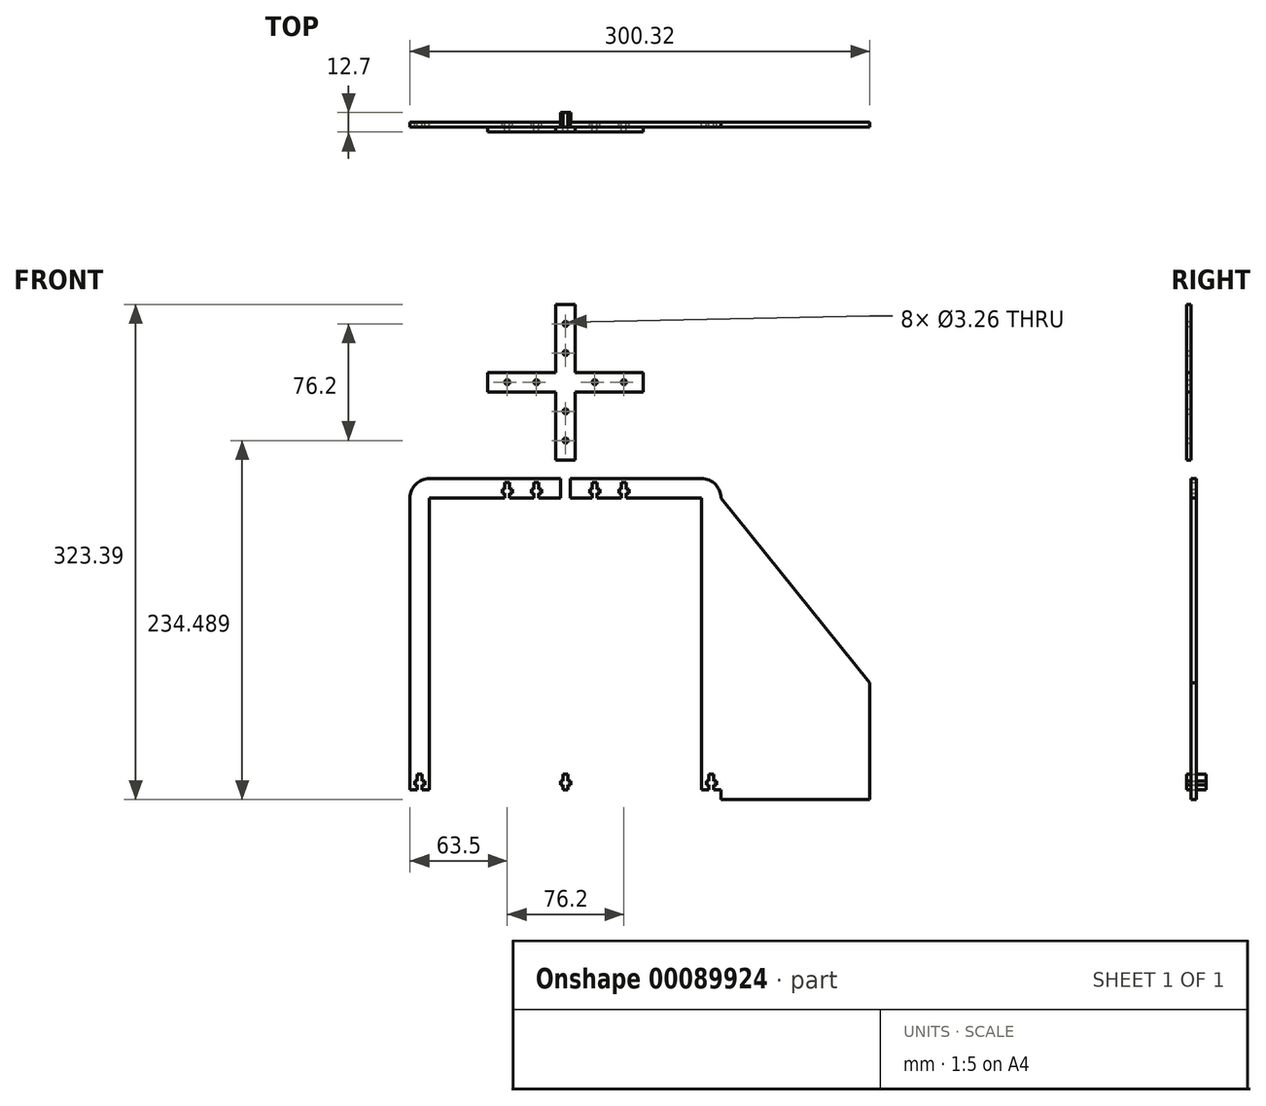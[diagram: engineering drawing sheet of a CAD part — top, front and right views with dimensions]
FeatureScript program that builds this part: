
annotation { "Feature Type Name" : "Feature", "Feature Type Description" : "" }
export const myFeature = defineFeature(function(context is Context, id is Id, definition is map)
    precondition{}
    {
        {
            var Q0;
            Q0=qCreatedBy(makeId("Top.planeOp"),FACE);
            var sketch = newSketch(context, id + "F0", { "sketchPlane" : qUnion([Q0])});
            skCircle(sketch, "E0", {"center": v(0, 0) * mm, "radius": 101.6 * mm});
            skSolve(sketch);
        }
        {
            var Q0;
            Q0=qCreatedBy(makeId("Front.planeOp"),FACE);
            var sketch = newSketch(context, id + "F1", { "sketchPlane" : qUnion([Q0])});
            skLineSegment(sketch, "E1", {"start": v(-101.6, 190.5) * mm, "end": v(-101.6, 0) * mm});
            skLineSegment(sketch, "E2", {"start": v(-88.9, 203.2) * mm, "end": v(-3.18, 203.2) * mm});
            skLineSegment(sketch, "E3", {"start": v(-3.18, 203.2) * mm, "end": v(-3.18, 190.5) * mm});
            skLineSegment(sketch, "E4", {"start": v(-3.18, 190.5) * mm, "end": v(-76.2, 190.5) * mm});
            skLineSegment(sketch, "E5", {"start": v(-88.9, 177.8) * mm, "end": v(-88.9, 0) * mm});
            skLineSegment(sketch, "E6", {"start": v(-88.9, 0) * mm, "end": v(-101.6, 0) * mm});
            skPoint(sketch, "E7.visualSharp", {"position": v(-88.9, 190.5) * mm});
            skPoint(sketch, "E8.visualSharp", {"position": v(-101.6, 203.2) * mm});
            skArc(sketch, "E8.filletArc", {"start": v(-88.9, 203.2) * mm, "mid": v(-97.88, 199.48) * mm, "end": v(-101.6, 190.5) * mm});
            skPoint(sketch, "E9.endSnap0", {"position": v(-95.25, 0) * mm});
            skLineSegment(sketch, "E10", {"start": v(-76.2, 190.5) * mm, "end": v(-88.9, 190.5) * mm});
            skLineSegment(sketch, "E11", {"start": v(-88.9, 177.8) * mm, "end": v(-88.9, 190.5) * mm});
            skSolve(sketch);
        }
        {
            var Q0;
            Q0=qCreatedBy(makeId("Front.planeOp"),FACE);
            var sketch = newSketch(context, id + "F2", { "sketchPlane" : qUnion([Q0])});
            skLineSegment(sketch, "E12", {"start": v(0, 0) * mm, "end": v(1.63, 0) * mm});
            skLineSegment(sketch, "E13", {"start": v(1.63, 0) * mm, "end": v(1.63, 3.18) * mm});
            skLineSegment(sketch, "E14", {"start": v(1.63, 3.18) * mm, "end": v(3.3, 3.18) * mm});
            skLineSegment(sketch, "E15", {"start": v(3.3, 3.18) * mm, "end": v(3.3, 5.72) * mm});
            skLineSegment(sketch, "E16", {"start": v(3.3, 5.72) * mm, "end": v(1.63, 5.72) * mm});
            skLineSegment(sketch, "E17", {"start": v(1.63, 5.72) * mm, "end": v(1.63, 10.16) * mm});
            skLineSegment(sketch, "E18", {"start": v(1.63, 10.16) * mm, "end": v(0, 10.16) * mm});
            skLineSegment(sketch, "E19.MirrorCS", {"start": v(-1.63, 0) * mm, "end": v(-1.63, 3.18) * mm});
            skLineSegment(sketch, "E20.MirrorCS", {"start": v(-1.63, 3.18) * mm, "end": v(-3.3, 3.18) * mm});
            skLineSegment(sketch, "E21.MirrorCS", {"start": v(-3.3, 3.18) * mm, "end": v(-3.3, 5.72) * mm});
            skLineSegment(sketch, "E22.MirrorCS", {"start": v(-3.3, 5.72) * mm, "end": v(-1.63, 5.72) * mm});
            skLineSegment(sketch, "E23.MirrorCS", {"start": v(-1.63, 10.16) * mm, "end": v(0, 10.16) * mm});
            skLineSegment(sketch, "E24.MirrorCS", {"start": v(-1.63, 5.72) * mm, "end": v(-1.63, 10.16) * mm});
            skLineSegment(sketch, "E25", {"start": v(0, 0) * mm, "end": v(-1.63, 0) * mm});
            skSolve(sketch);
        }
        {
            var Q0;
            Q0=makeQuery(id+"F2.imprint","IMPRINT",FACE,{"disambiguationData":[TD([[makeQuery(id+"F2.imprint","IMPRINT",EDGE,{"derivedFrom":sQuery(id+"F2.wireOp",EDGE,"E12")}),1.0]])]});
            extrude(context, id + "F3", {"entities" : qUnion([Q0]), "endBound" : BoundingType.SYMMETRIC, "depth" : 12.7 * mm});
        }
        {
            var Q0;
            Q0=makeQuery(id+"F1.imprint","IMPRINT",FACE,{"disambiguationData":[TD([[makeQuery(id+"F1.imprint","IMPRINT",EDGE,{"derivedFrom":sQuery(id+"F1.wireOp",EDGE,"E1")}),1.0]])]});
            extrude(context, id + "F4", {"entities" : qUnion([Q0]), "depth" : 3.17 * mm});
        }
        {
            var Q0;
            Q0=makeQuery(id+"F3.opExtrude","SWEPT_BODY",BODY,{"disambiguationData":[OSD([sQuery(id+"F2.wireOp",EDGE,"E12"),sQuery(id+"F2.wireOp",EDGE,"E13"),sQuery(id+"F2.wireOp",EDGE,"E14"),sQuery(id+"F2.wireOp",EDGE,"E15"),sQuery(id+"F2.wireOp",EDGE,"E16"),sQuery(id+"F2.wireOp",EDGE,"E17"),sQuery(id+"F2.wireOp",EDGE,"E18"),sQuery(id+"F2.wireOp",EDGE,"E19.MirrorCS"),sQuery(id+"F2.wireOp",EDGE,"E20.MirrorCS"),sQuery(id+"F2.wireOp",EDGE,"E21.MirrorCS"),sQuery(id+"F2.wireOp",EDGE,"E22.MirrorCS"),sQuery(id+"F2.wireOp",EDGE,"E23.MirrorCS"),sQuery(id+"F2.wireOp",EDGE,"E24.MirrorCS"),sQuery(id+"F2.wireOp",EDGE,"E25")])]});
            transform(context, id + "F5", {"entities" : qUnion([Q0]), "transformType" : TransformType.TRANSLATION_3D, "dx" : -95.25 * mm, "dy" : 0 * mm, "dz" : 0 * mm, "makeCopy" : true});
        }
        {
            var Q0;
            Q0=makeQuery(id+"F5.opPattern","COPY",BODY,{"derivedFrom":makeQuery(id+"F3.opExtrude","SWEPT_BODY",BODY,{"disambiguationData":[OSD([sQuery(id+"F2.wireOp",EDGE,"E12"),sQuery(id+"F2.wireOp",EDGE,"E13"),sQuery(id+"F2.wireOp",EDGE,"E14"),sQuery(id+"F2.wireOp",EDGE,"E15"),sQuery(id+"F2.wireOp",EDGE,"E16"),sQuery(id+"F2.wireOp",EDGE,"E17"),sQuery(id+"F2.wireOp",EDGE,"E18"),sQuery(id+"F2.wireOp",EDGE,"E19.MirrorCS"),sQuery(id+"F2.wireOp",EDGE,"E20.MirrorCS"),sQuery(id+"F2.wireOp",EDGE,"E21.MirrorCS"),sQuery(id+"F2.wireOp",EDGE,"E22.MirrorCS"),sQuery(id+"F2.wireOp",EDGE,"E23.MirrorCS"),sQuery(id+"F2.wireOp",EDGE,"E24.MirrorCS"),sQuery(id+"F2.wireOp",EDGE,"E25")])]}),"instanceName":"1"});
            var Q1;
            Q1=makeQuery(id+"F4.opExtrude","SWEPT_BODY",BODY,{"disambiguationData":[OSD([sQuery(id+"F1.wireOp",EDGE,"E1"),sQuery(id+"F1.wireOp",EDGE,"E2"),sQuery(id+"F1.wireOp",EDGE,"E3"),sQuery(id+"F1.wireOp",EDGE,"E4"),sQuery(id+"F1.wireOp",EDGE,"E5"),sQuery(id+"F1.wireOp",EDGE,"E6"),sQuery(id+"F1.wireOp",EDGE,"E7.filletArc"),sQuery(id+"F1.wireOp",EDGE,"E8.filletArc")])]});
            booleanBodies(context, id + "F6", {"operationType" : BooleanOperationType.SUBTRACTION, "tools" : qUnion([Q0]), "targets" : qUnion([Q1])});
        }
        {
            var Q0;
            Q0=makeQuery(id+"F3.opExtrude","SWEPT_BODY",BODY,{"disambiguationData":[OSD([sQuery(id+"F2.wireOp",EDGE,"E12"),sQuery(id+"F2.wireOp",EDGE,"E13"),sQuery(id+"F2.wireOp",EDGE,"E14"),sQuery(id+"F2.wireOp",EDGE,"E15"),sQuery(id+"F2.wireOp",EDGE,"E16"),sQuery(id+"F2.wireOp",EDGE,"E17"),sQuery(id+"F2.wireOp",EDGE,"E18"),sQuery(id+"F2.wireOp",EDGE,"E19.MirrorCS"),sQuery(id+"F2.wireOp",EDGE,"E20.MirrorCS"),sQuery(id+"F2.wireOp",EDGE,"E21.MirrorCS"),sQuery(id+"F2.wireOp",EDGE,"E22.MirrorCS"),sQuery(id+"F2.wireOp",EDGE,"E23.MirrorCS"),sQuery(id+"F2.wireOp",EDGE,"E24.MirrorCS"),sQuery(id+"F2.wireOp",EDGE,"E25")])]});
            transform(context, id + "F7", {"entities" : qUnion([Q0]), "transformType" : TransformType.TRANSLATION_3D, "dx" : -19.05 * mm, "dy" : 0 * mm, "dz" : 190.5 * mm, "makeCopy" : true});
        }
        {
            var Q0;
            Q0=makeQuery(id+"F7.opPattern","COPY",BODY,{"derivedFrom":makeQuery(id+"F3.opExtrude","SWEPT_BODY",BODY,{"disambiguationData":[OSD([sQuery(id+"F2.wireOp",EDGE,"E12"),sQuery(id+"F2.wireOp",EDGE,"E13"),sQuery(id+"F2.wireOp",EDGE,"E14"),sQuery(id+"F2.wireOp",EDGE,"E15"),sQuery(id+"F2.wireOp",EDGE,"E16"),sQuery(id+"F2.wireOp",EDGE,"E17"),sQuery(id+"F2.wireOp",EDGE,"E18"),sQuery(id+"F2.wireOp",EDGE,"E19.MirrorCS"),sQuery(id+"F2.wireOp",EDGE,"E20.MirrorCS"),sQuery(id+"F2.wireOp",EDGE,"E21.MirrorCS"),sQuery(id+"F2.wireOp",EDGE,"E22.MirrorCS"),sQuery(id+"F2.wireOp",EDGE,"E23.MirrorCS"),sQuery(id+"F2.wireOp",EDGE,"E24.MirrorCS"),sQuery(id+"F2.wireOp",EDGE,"E25")])]}),"instanceName":"1"});
            var Q1;
            Q1=makeQuery(id+"F4.opExtrude","SWEPT_BODY",BODY,{"disambiguationData":[OSD([sQuery(id+"F1.wireOp",EDGE,"E1"),sQuery(id+"F1.wireOp",EDGE,"E2"),sQuery(id+"F1.wireOp",EDGE,"E3"),sQuery(id+"F1.wireOp",EDGE,"E4"),sQuery(id+"F1.wireOp",EDGE,"E5"),sQuery(id+"F1.wireOp",EDGE,"E6"),sQuery(id+"F1.wireOp",EDGE,"E7.filletArc"),sQuery(id+"F1.wireOp",EDGE,"E8.filletArc")])]});
            booleanBodies(context, id + "F8", {"operationType" : BooleanOperationType.SUBTRACTION, "tools" : qUnion([Q0]), "targets" : qUnion([Q1])});
        }
        {
            var Q0;
            Q0=makeQuery(id+"F3.opExtrude","SWEPT_BODY",BODY,{"disambiguationData":[OSD([sQuery(id+"F2.wireOp",EDGE,"E12"),sQuery(id+"F2.wireOp",EDGE,"E13"),sQuery(id+"F2.wireOp",EDGE,"E14"),sQuery(id+"F2.wireOp",EDGE,"E15"),sQuery(id+"F2.wireOp",EDGE,"E16"),sQuery(id+"F2.wireOp",EDGE,"E17"),sQuery(id+"F2.wireOp",EDGE,"E18"),sQuery(id+"F2.wireOp",EDGE,"E19.MirrorCS"),sQuery(id+"F2.wireOp",EDGE,"E20.MirrorCS"),sQuery(id+"F2.wireOp",EDGE,"E21.MirrorCS"),sQuery(id+"F2.wireOp",EDGE,"E22.MirrorCS"),sQuery(id+"F2.wireOp",EDGE,"E23.MirrorCS"),sQuery(id+"F2.wireOp",EDGE,"E24.MirrorCS"),sQuery(id+"F2.wireOp",EDGE,"E25")])]});
            transform(context, id + "F9", {"entities" : qUnion([Q0]), "transformType" : TransformType.TRANSLATION_3D, "dx" : -38.1 * mm, "dy" : 0 * mm, "dz" : 190.5 * mm, "makeCopy" : true});
        }
        {
            var Q0;
            Q0=makeQuery(id+"F9.opPattern","COPY",BODY,{"derivedFrom":makeQuery(id+"F3.opExtrude","SWEPT_BODY",BODY,{"disambiguationData":[OSD([sQuery(id+"F2.wireOp",EDGE,"E12"),sQuery(id+"F2.wireOp",EDGE,"E13"),sQuery(id+"F2.wireOp",EDGE,"E14"),sQuery(id+"F2.wireOp",EDGE,"E15"),sQuery(id+"F2.wireOp",EDGE,"E16"),sQuery(id+"F2.wireOp",EDGE,"E17"),sQuery(id+"F2.wireOp",EDGE,"E18"),sQuery(id+"F2.wireOp",EDGE,"E19.MirrorCS"),sQuery(id+"F2.wireOp",EDGE,"E20.MirrorCS"),sQuery(id+"F2.wireOp",EDGE,"E21.MirrorCS"),sQuery(id+"F2.wireOp",EDGE,"E22.MirrorCS"),sQuery(id+"F2.wireOp",EDGE,"E23.MirrorCS"),sQuery(id+"F2.wireOp",EDGE,"E24.MirrorCS"),sQuery(id+"F2.wireOp",EDGE,"E25")])]}),"instanceName":"1"});
            var Q1;
            Q1=makeQuery(id+"F4.opExtrude","SWEPT_BODY",BODY,{"disambiguationData":[OSD([sQuery(id+"F1.wireOp",EDGE,"E1"),sQuery(id+"F1.wireOp",EDGE,"E2"),sQuery(id+"F1.wireOp",EDGE,"E3"),sQuery(id+"F1.wireOp",EDGE,"E4"),sQuery(id+"F1.wireOp",EDGE,"E5"),sQuery(id+"F1.wireOp",EDGE,"E6"),sQuery(id+"F1.wireOp",EDGE,"E7.filletArc"),sQuery(id+"F1.wireOp",EDGE,"E8.filletArc")])]});
            booleanBodies(context, id + "F10", {"operationType" : BooleanOperationType.SUBTRACTION, "tools" : qUnion([Q0]), "targets" : qUnion([Q1])});
        }
        {
            var Q0;
            Q0=makeQuery(id+"F4.opExtrude","SWEPT_BODY",BODY,{"disambiguationData":[OSD([sQuery(id+"F1.wireOp",EDGE,"E1"),sQuery(id+"F1.wireOp",EDGE,"E2"),sQuery(id+"F1.wireOp",EDGE,"E3"),sQuery(id+"F1.wireOp",EDGE,"E4"),sQuery(id+"F1.wireOp",EDGE,"E5"),sQuery(id+"F1.wireOp",EDGE,"E6"),sQuery(id+"F1.wireOp",EDGE,"E8.filletArc"),sQuery(id+"F1.wireOp",EDGE,"E10"),sQuery(id+"F1.wireOp",EDGE,"E11")])]});
            var Q1;
            Q1=qCreatedBy(makeId("Right.planeOp"),FACE);
            mirror(context, id + "F11", {"entities" : qUnion([Q0]), "mirrorPlane" : qUnion([Q1])});
        }
        {
            var Q0;
            Q0=makeQuery(id+"F11.opPattern","COPY",FACE,{"derivedFrom":makeQuery(id+"F4.opExtrude","CAP_FACE",FACE,{"disambiguationData":[OSD([sQuery(id+"F1.wireOp",EDGE,"E1"),sQuery(id+"F1.wireOp",EDGE,"E2"),sQuery(id+"F1.wireOp",EDGE,"E3"),sQuery(id+"F1.wireOp",EDGE,"E4"),sQuery(id+"F1.wireOp",EDGE,"E5"),sQuery(id+"F1.wireOp",EDGE,"E6"),sQuery(id+"F1.wireOp",EDGE,"E8.filletArc"),sQuery(id+"F1.wireOp",EDGE,"E10"),sQuery(id+"F1.wireOp",EDGE,"E11")])],"isStart":false}),"instanceName":"1"});
            var sketch = newSketch(context, id + "F12", { "sketchPlane" : qUnion([Q0])});
            skLineSegment(sketch, "E26", {"start": v(101.6, 190.5) * mm, "end": v(198.72, 69.85) * mm});
            skLineSegment(sketch, "E27", {"start": v(198.72, 69.85) * mm, "end": v(198.72, 0) * mm});
            skLineSegment(sketch, "E28", {"start": v(198.72, 0) * mm, "end": v(198.72, -6.35) * mm});
            skLineSegment(sketch, "E29", {"start": v(198.72, -6.35) * mm, "end": v(101.6, -6.35) * mm});
            skLineSegment(sketch, "E30", {"start": v(101.6, -6.35) * mm, "end": v(101.6, 0) * mm});
            skLineSegment(sketch, "E31", {"start": v(101.6, 0) * mm, "end": v(101.6, 190.5) * mm});
            skSolve(sketch);
        }
        {
            var Q0;
            Q0=makeQuery(id+"F12.imprint","IMPRINT",FACE,{"disambiguationData":[TD([[makeQuery(id+"F12.imprint","IMPRINT",EDGE,{"derivedFrom":sQuery(id+"F12.wireOp",EDGE,"E26")}),-1.0]])]});
            extrude(context, id + "F13", {"entities" : qUnion([Q0]), "operationType" : NewBodyOperationType.ADD, "oppositeDirection" : true, "depth" : 3.17 * mm});
        }
        {
            var Q0;
            Q0=makeQuery(id+"F4.opExtrude","CAP_FACE",FACE,{"disambiguationData":[OSD([sQuery(id+"F1.wireOp",EDGE,"E1"),sQuery(id+"F1.wireOp",EDGE,"E2"),sQuery(id+"F1.wireOp",EDGE,"E3"),sQuery(id+"F1.wireOp",EDGE,"E4"),sQuery(id+"F1.wireOp",EDGE,"E5"),sQuery(id+"F1.wireOp",EDGE,"E6"),sQuery(id+"F1.wireOp",EDGE,"E8.filletArc"),sQuery(id+"F1.wireOp",EDGE,"E10"),sQuery(id+"F1.wireOp",EDGE,"E11")])],"isStart":false});
            var sketch = newSketch(context, id + "F14", { "sketchPlane" : qUnion([Q0])});
            skLineSegment(sketch, "E32", {"start": v(-19.05, 200.66) * mm, "end": v(-19.05, 336.22) * mm, "construction": true});
            skLineSegment(sketch, "E33", {"start": v(-38.1, 200.66) * mm, "end": v(-38.1, 336.22) * mm, "construction": true});
            skLineSegment(sketch, "E34", {"start": v(0, 259.89) * mm, "end": v(-50.8, 259.89) * mm});
            skLineSegment(sketch, "E35", {"start": v(-50.8, 259.89) * mm, "end": v(-50.8, 272.59) * mm});
            skLineSegment(sketch, "E36", {"start": v(-50.8, 272.59) * mm, "end": v(0, 272.59) * mm});
            skLineSegment(sketch, "E37", {"start": v(-50.8, 266.24) * mm, "end": v(-2.03, 266.24) * mm, "construction": true});
            skCircle(sketch, "E38", {"center": v(-38.1, 266.24) * mm, "radius": 1.63 * mm});
            skCircle(sketch, "E39", {"center": v(-19.05, 266.24) * mm, "radius": 1.63 * mm});
            skLineSegment(sketch, "E40.1.0", {"start": v(6.35, 266.24) * mm, "end": v(6.35, 215.44) * mm});
            skLineSegment(sketch, "E40.1.1", {"start": v(6.35, 215.44) * mm, "end": v(-6.35, 215.44) * mm});
            skLineSegment(sketch, "E40.1.2", {"start": v(-6.35, 215.44) * mm, "end": v(-6.35, 266.24) * mm});
            skCircle(sketch, "E40.1.3", {"center": v(0, 228.14) * mm, "radius": 1.63 * mm});
            skCircle(sketch, "E40.1.4", {"center": v(0, 247.19) * mm, "radius": 1.63 * mm});
            skLineSegment(sketch, "E40.2.0", {"start": v(0, 272.59) * mm, "end": v(50.8, 272.59) * mm});
            skLineSegment(sketch, "E40.2.1", {"start": v(50.8, 272.59) * mm, "end": v(50.8, 259.89) * mm});
            skLineSegment(sketch, "E40.2.2", {"start": v(50.8, 259.89) * mm, "end": v(0, 259.89) * mm});
            skCircle(sketch, "E40.2.3", {"center": v(38.1, 266.24) * mm, "radius": 1.63 * mm});
            skCircle(sketch, "E40.2.4", {"center": v(19.05, 266.24) * mm, "radius": 1.63 * mm});
            skLineSegment(sketch, "E40.3.0", {"start": v(-6.35, 266.24) * mm, "end": v(-6.35, 317.04) * mm});
            skLineSegment(sketch, "E40.3.1", {"start": v(-6.35, 317.04) * mm, "end": v(6.35, 317.04) * mm});
            skLineSegment(sketch, "E40.3.2", {"start": v(6.35, 317.04) * mm, "end": v(6.35, 266.24) * mm});
            skCircle(sketch, "E40.3.3", {"center": v(0, 304.34) * mm, "radius": 1.63 * mm});
            skCircle(sketch, "E40.3.4", {"center": v(0, 285.29) * mm, "radius": 1.63 * mm});
            skPoint(sketch, "E40.center", {"position": v(0, 266.24) * mm});
            skSolve(sketch);
        }
        {
            var Q0;
            {var subQ0=sQuery(id+"F14.wireOp",EDGE,"E40.1.1");Q0=makeQuery(id+"F14.imprint","IMPRINT",FACE,{"disambiguationData":[TD([[makeQuery(id+"F14.imprint","IMPRINT",EDGE,{"derivedFrom":subQ0}),-1.0]])]});}
            var Q1;
            {var subQ0=sQuery(id+"F14.wireOp",EDGE,"E35");Q1=makeQuery(id+"F14.imprint","IMPRINT",FACE,{"disambiguationData":[TD([[makeQuery(id+"F14.imprint","IMPRINT",EDGE,{"derivedFrom":subQ0}),-1.0]])]});}
            var Q2;
            {var subQ3=sQuery(id+"F14.wireOp",EDGE,"E34");var subQ10=sQuery(id+"F14.wireOp",EDGE,"E40.2.2");var subQ15=makeQuery(id+"F14.imprint","INTERSECT",VERTEX,{"derivedFrom":[subQ3,subQ10]});Q2=makeQuery(id+"F14.imprint","IMPRINT",FACE,{"disambiguationData":[TD([[makeQuery(id+"F14.imprint","IMPRINT",EDGE,{"disambiguationData":[TD([[subQ15,-1.0]])],"derivedFrom":subQ3}),-1.0]])]});}
            var Q3;
            {var subQ1=sQuery(id+"F14.wireOp",EDGE,"E40.2.1");Q3=makeQuery(id+"F14.imprint","IMPRINT",FACE,{"disambiguationData":[TD([[makeQuery(id+"F14.imprint","IMPRINT",EDGE,{"derivedFrom":subQ1}),-1.0]])]});}
            var Q4;
            {var subQ0=sQuery(id+"F14.wireOp",EDGE,"E40.3.1");Q4=makeQuery(id+"F14.imprint","IMPRINT",FACE,{"disambiguationData":[TD([[makeQuery(id+"F14.imprint","IMPRINT",EDGE,{"derivedFrom":subQ0}),-1.0]])]});}
            extrude(context, id + "F15", {"entities" : qUnion([Q0, Q1, Q2, Q3, Q4]), "depth" : 3.17 * mm});
        }
    });
